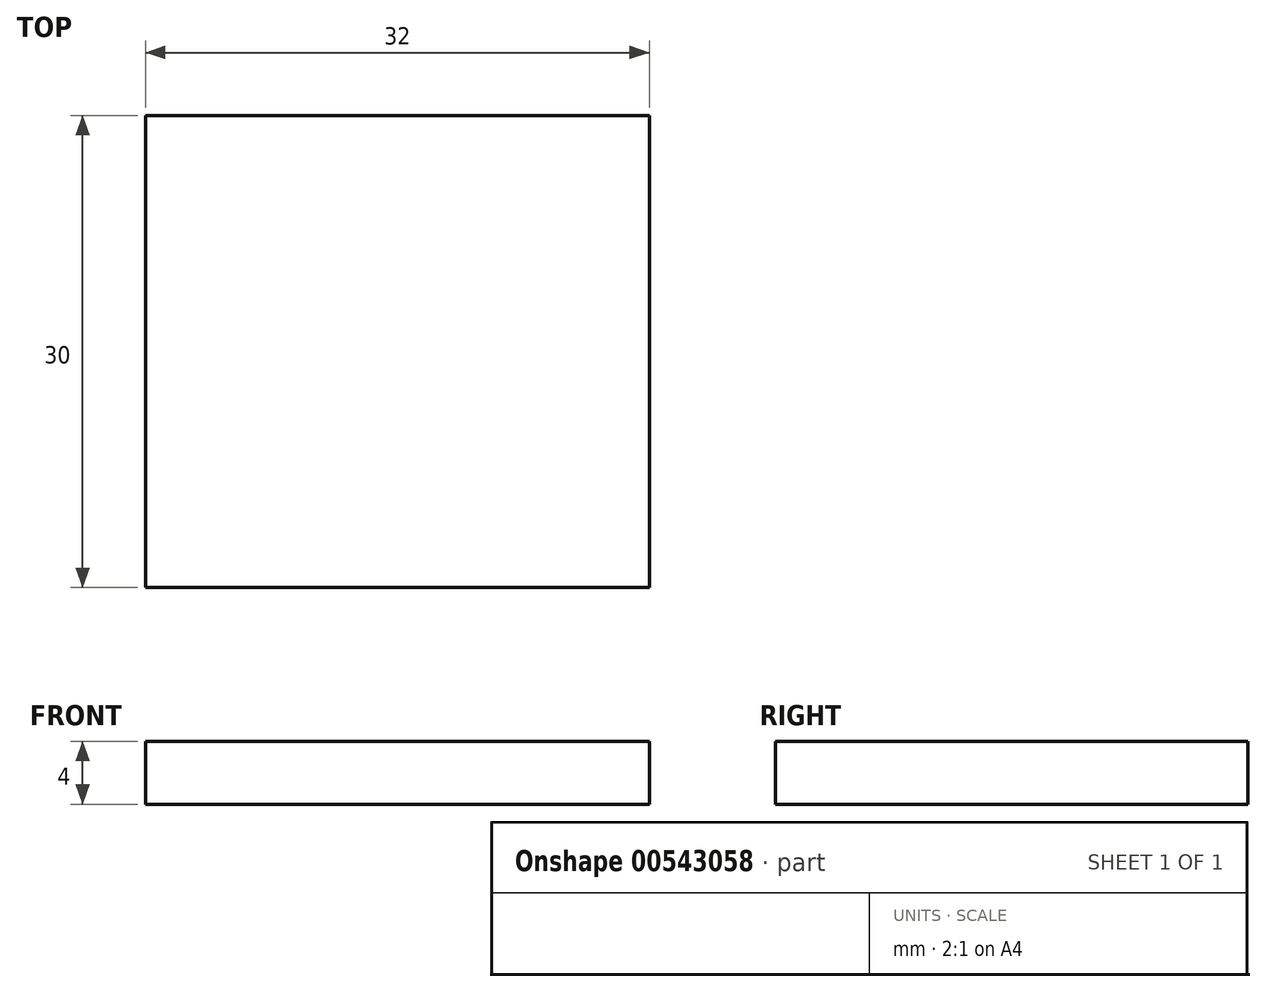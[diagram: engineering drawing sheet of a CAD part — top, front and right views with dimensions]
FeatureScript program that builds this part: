
annotation { "Feature Type Name" : "Feature", "Feature Type Description" : "" }
export const myFeature = defineFeature(function(context is Context, id is Id, definition is map)
    precondition{}
    {
        {
            var Q0;
            Q0=qCreatedBy(makeId("Top.planeOp"),FACE);
            var sketch = newSketch(context, id + "F0", { "sketchPlane" : qUnion([Q0])});
            skLineSegment(sketch, "E0.bottom", {"start": v(-16, -15) * mm, "end": v(16, -15) * mm});
            skLineSegment(sketch, "E0.top", {"start": v(-16, 15) * mm, "end": v(16, 15) * mm});
            skLineSegment(sketch, "E0.left", {"start": v(-16, -15) * mm, "end": v(-16, 15) * mm});
            skLineSegment(sketch, "E0.right", {"start": v(16, -15) * mm, "end": v(16, 15) * mm});
            skPoint(sketch, "E0.middle", {"position": v(0, 0) * mm});
            skSolve(sketch);
        }
        {
            var Q0;
            Q0=makeQuery(id+"F0.imprint","IMPRINT",FACE,{"disambiguationData":[TD([[makeQuery(id+"F0.imprint","IMPRINT",EDGE,{"derivedFrom":sQuery(id+"F0.wireOp",EDGE,"E0.bottom")}),1.0]])]});
            extrude(context, id + "F1", {"entities" : qUnion([Q0]), "depth" : 4 * mm, "offsetDistance" : 25 * mm});
        }
    });
